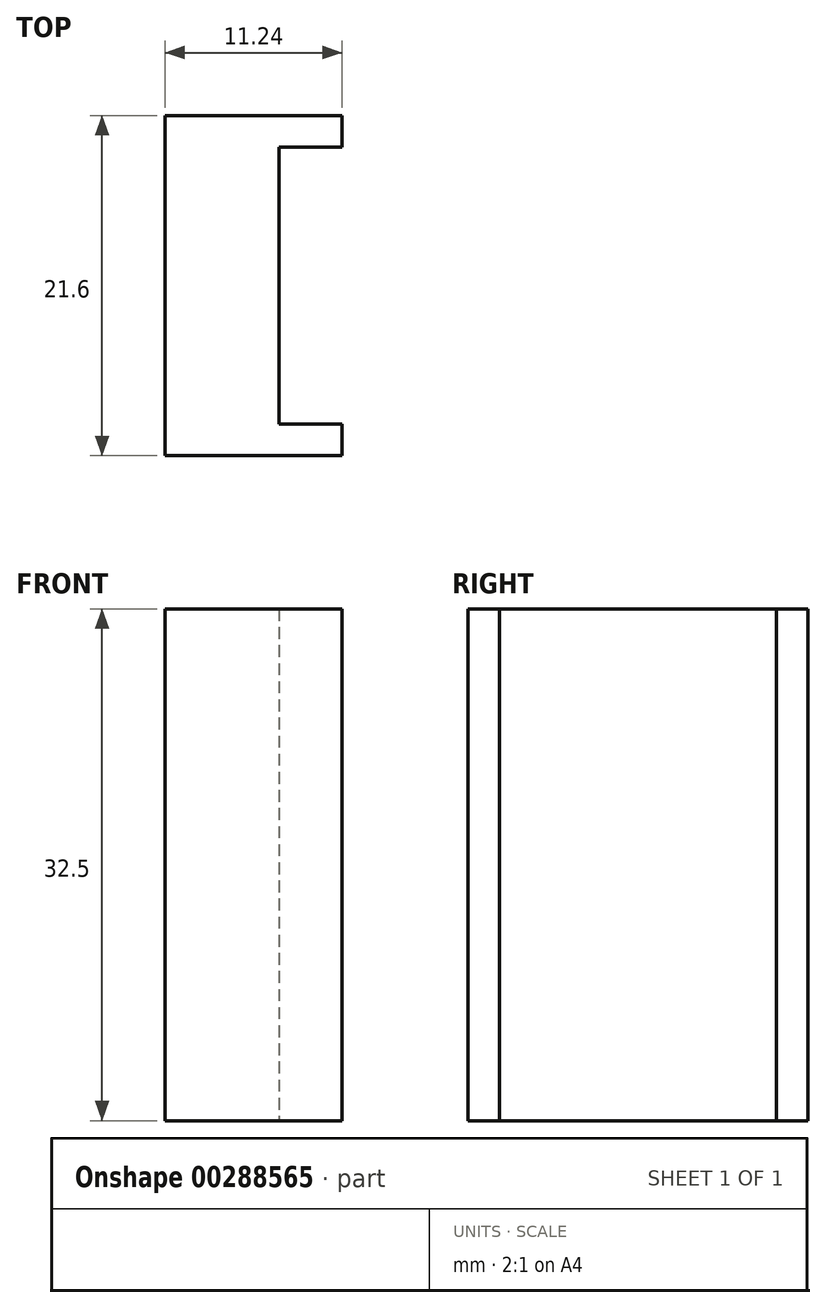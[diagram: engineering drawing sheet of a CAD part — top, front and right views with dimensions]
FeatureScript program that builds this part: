
annotation { "Feature Type Name" : "Feature", "Feature Type Description" : "" }
export const myFeature = defineFeature(function(context is Context, id is Id, definition is map)
    precondition{}
    {
        {
            var Q0;
            Q0=qCreatedBy(makeId("Top.planeOp"),FACE);
            var sketch = newSketch(context, id + "F0", { "sketchPlane" : qUnion([Q0])});
            skLineSegment(sketch, "E0.bottom", {"start": v(3.63, 10.8) * mm, "end": v(-3.62, 10.8) * mm});
            skLineSegment(sketch, "E0.top", {"start": v(3.62, -10.8) * mm, "end": v(-3.63, -10.8) * mm});
            skLineSegment(sketch, "E0.left", {"start": v(3.63, 10.8) * mm, "end": v(3.62, -10.8) * mm});
            skLineSegment(sketch, "E0.right", {"start": v(-3.62, 10.8) * mm, "end": v(-3.63, -10.8) * mm});
            skPoint(sketch, "E0.middle", {"position": v(0, 0) * mm});
            skLineSegment(sketch, "E1.bottom", {"start": v(3.63, 10.8) * mm, "end": v(7.62, 10.8) * mm});
            skLineSegment(sketch, "E1.top", {"start": v(3.62, 8.8) * mm, "end": v(7.62, 8.8) * mm});
            skLineSegment(sketch, "E1.left", {"start": v(3.63, 10.8) * mm, "end": v(3.63, 8.8) * mm});
            skLineSegment(sketch, "E1.right", {"start": v(7.63, 10.8) * mm, "end": v(7.63, 8.8) * mm});
            skLineSegment(sketch, "E2.MirrorCS", {"start": v(3.62, -8.8) * mm, "end": v(7.62, -8.8) * mm});
            skLineSegment(sketch, "E3.MirrorCS", {"start": v(3.63, -10.8) * mm, "end": v(7.62, -10.8) * mm});
            skLineSegment(sketch, "E4.MirrorCS", {"start": v(7.62, -10.8) * mm, "end": v(7.62, -8.8) * mm});
            skSolve(sketch);
        }
        {
            var Q0;
            {var subQ1=sQuery(id+"F0.wireOp",EDGE,"E0.bottom");Q0=makeQuery(id+"F0.imprint","IMPRINT",FACE,{"disambiguationData":[TD([[makeQuery(id+"F0.imprint","IMPRINT",EDGE,{"derivedFrom":subQ1}),1.0]])]});}
            var Q1;
            {var subQ0=sQuery(id+"F0.wireOp",EDGE,"E1.bottom");Q1=makeQuery(id+"F0.imprint","IMPRINT",FACE,{"disambiguationData":[TD([[makeQuery(id+"F0.imprint","IMPRINT",EDGE,{"derivedFrom":subQ0}),-1.0]])]});}
            var Q2;
            {var subQ2=sQuery(id+"F0.wireOp",EDGE,"E2.MirrorCS");Q2=makeQuery(id+"F0.imprint","IMPRINT",FACE,{"disambiguationData":[TD([[makeQuery(id+"F0.imprint","IMPRINT",EDGE,{"derivedFrom":subQ2}),-1.0]])]});}
            extrude(context, id + "F1", {"entities" : qUnion([Q0, Q1, Q2]), "depth" : 32.5 * mm, "offsetDistance" : 25 * mm});
        }
    });
